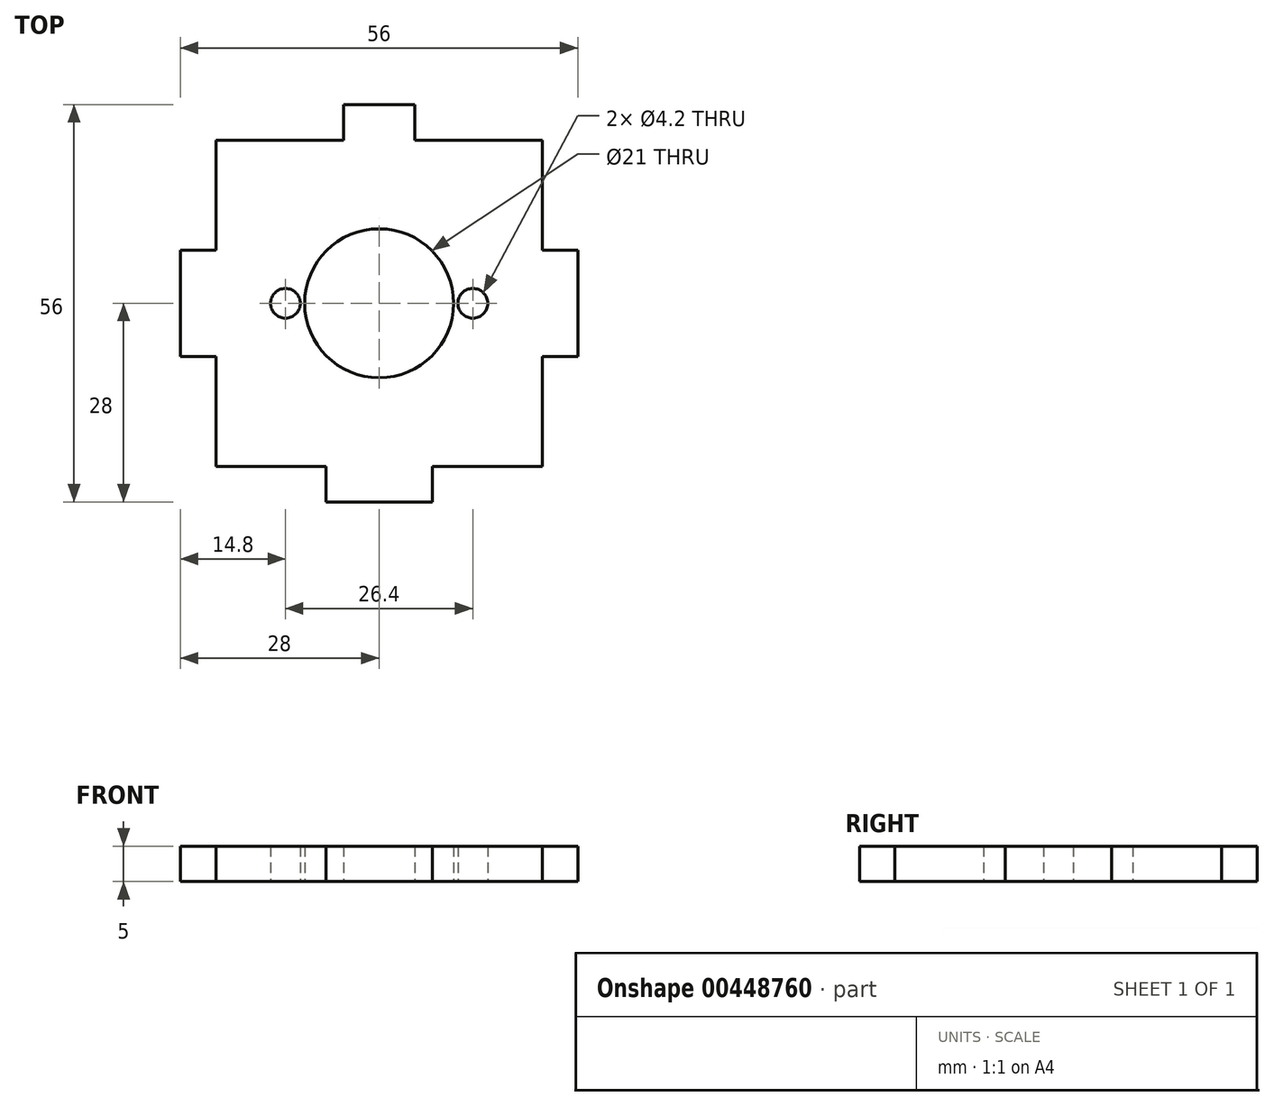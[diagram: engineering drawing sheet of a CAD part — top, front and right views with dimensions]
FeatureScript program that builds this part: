
annotation { "Feature Type Name" : "Feature", "Feature Type Description" : "" }
export const myFeature = defineFeature(function(context is Context, id is Id, definition is map)
    precondition{}
    {
        {
            assignVariable(context, id + "F0", {"name" : "thickness", "anyValue" : 5 * mm});
        }
        {
            var Q0;
            Q0=qCreatedBy(makeId("Top.planeOp"),FACE);
            var sketch = newSketch(context, id + "F1", { "sketchPlane" : qUnion([Q0])});
            skLineSegment(sketch, "E0.bottom", {"start": v(0, 0) * mm, "end": v(15.5, 0) * mm});
            skLineSegment(sketch, "E0.top", {"start": v(0, 46) * mm, "end": v(18, 46) * mm});
            skLineSegment(sketch, "E0.left", {"start": v(0, 0) * mm, "end": v(0, 15.5) * mm});
            skLineSegment(sketch, "E0.right", {"start": v(46, 0) * mm, "end": v(46, 15.5) * mm});
            skCircle(sketch, "E1", {"center": v(23, 23) * mm, "radius": 13.2 * mm, "construction": true});
            skPoint(sketch, "E1.centerSnap0", {"position": v(0, 23) * mm});
            skPoint(sketch, "E1.centerSnap1", {"position": v(23, 46) * mm});
            skCircle(sketch, "E2", {"center": v(23, 23) * mm, "radius": 10.5 * mm});
            skLineSegment(sketch, "E3", {"start": v(18, 46) * mm, "end": v(18, 51) * mm});
            skLineSegment(sketch, "E4", {"start": v(18, 51) * mm, "end": v(28, 51) * mm});
            skLineSegment(sketch, "E5", {"start": v(28, 51) * mm, "end": v(28, 46) * mm});
            skPoint(sketch, "E6", {"position": v(23, 51) * mm});
            skLineSegment(sketch, "E7.trimOffspring", {"start": v(28, 46) * mm, "end": v(46, 46) * mm});
            skLineSegment(sketch, "E8", {"start": v(0, 30.5) * mm, "end": v(-5, 30.5) * mm});
            skLineSegment(sketch, "E9", {"start": v(-5, 30.5) * mm, "end": v(-5, 15.5) * mm});
            skLineSegment(sketch, "E10", {"start": v(-5, 15.5) * mm, "end": v(0, 15.5) * mm});
            skPoint(sketch, "E11", {"position": v(-5, 23) * mm});
            skLineSegment(sketch, "E12", {"start": v(23, 51) * mm, "end": v(23, 0) * mm, "construction": true});
            skPoint(sketch, "E13.MirrorP", {"position": v(46, 23) * mm});
            skLineSegment(sketch, "E14.MirrorCS", {"start": v(51, 15.5) * mm, "end": v(46, 15.5) * mm});
            skLineSegment(sketch, "E15.MirrorCS", {"start": v(51, 30.5) * mm, "end": v(51, 15.5) * mm});
            skLineSegment(sketch, "E16.MirrorCS", {"start": v(46, 30.5) * mm, "end": v(51, 30.5) * mm});
            skPoint(sketch, "E17.MirrorP", {"position": v(51, 23) * mm});
            skLineSegment(sketch, "E18.trimOffspring", {"start": v(0, 30.5) * mm, "end": v(0, 46) * mm});
            skLineSegment(sketch, "E19.trimOffspring", {"start": v(46, 30.5) * mm, "end": v(46, 46) * mm});
            skLineSegment(sketch, "E20", {"start": v(0, 0) * mm, "end": v(46, 46) * mm, "construction": true});
            skPoint(sketch, "E21.MirrorP", {"position": v(23, 0) * mm});
            skLineSegment(sketch, "E22.MirrorCS", {"start": v(15.5, -5) * mm, "end": v(15.5, 0) * mm});
            skLineSegment(sketch, "E23.MirrorCS", {"start": v(30.5, -5) * mm, "end": v(15.5, -5) * mm});
            skLineSegment(sketch, "E24.MirrorCS", {"start": v(30.5, 0) * mm, "end": v(30.5, -5) * mm});
            skPoint(sketch, "E25.MirrorP", {"position": v(23, -5) * mm});
            skLineSegment(sketch, "E26.trimOffspring", {"start": v(30.5, 0) * mm, "end": v(46, 0) * mm});
            skCircle(sketch, "E27", {"center": v(9.8, 23) * mm, "radius": 2.1 * mm});
            skCircle(sketch, "E28.MirrorC", {"center": v(36.2, 23) * mm, "radius": 2.1 * mm});
            skSolve(sketch);
        }
        {
            var Q0;
            Q0=qSketchRegion(id+"F1",true);
            extrude(context, id + "F2", {"entities" : qUnion([Q0]), "depth" : getVariable(context, 'thickness')});
        }
    });
